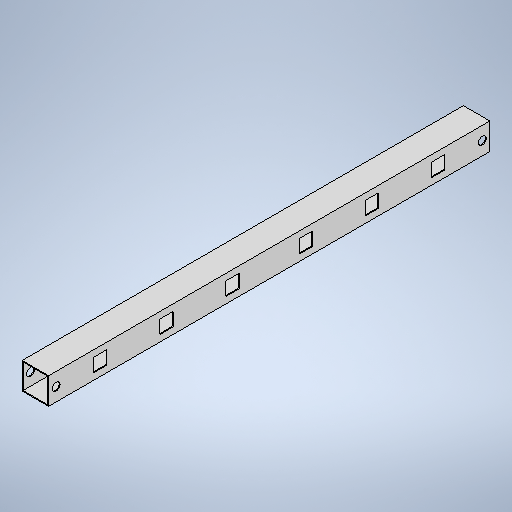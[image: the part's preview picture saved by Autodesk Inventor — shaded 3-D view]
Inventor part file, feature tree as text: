
AUTODESK INVENTOR PART (.ipt)
format: ipt  version: 2025.1 (Build 291241020, 241B)  size: 515,072 bytes
history: native  units: mm
features: sketch x5, extrude x3, projected_geometry x3, fillet x2, mirror x1
ambient origin geometry x8: Origin, YZ Plane, XZ Plane, XY Plane, X Axis, Y Axis, Z Axis, Center Point
bodies: Body1 (feature_tree)
feature tree (14):
  extrude  "Extrusion3"  Depth=60.0mm
  extrude  "Extrusion4"  Depth=2.0mm
  fillet  "Fillet1"  Radius=500.0mm
  mirror  "Mirror1"
  extrude  "Extrusion5"  Depth=30.5mm
  fillet  "Fillet2"  [1 undecoded]
  sketch  "Sketch15"  dims[d181=47.0mm]
  sketch  "Sketch16"  dims[d182=130.0mm d183=280.0mm d184=430.0mm d185=530.0mm d186=18.0mm d187=2.0mm d188=54.0mm d189=500.0mm d190=0.0mm d191=2.0mm]
  sketch  "Sketch9"  dims[d61=500.0mm d172=60.0mm]
  sketch  "Sketch10"  dims[d173=60.0mm d174=2.0mm d175=500.0mm d176=0.0mm]
  projected_geometry  "Projected Loop3"
  sketch  "Sketch14"  dims[d177=30.5mm d178=30.5mm d179=0.0mm d180=0.0mm]
  projected_geometry  "Projected Loop6"
  projected_geometry  "Projected Loop7"
note: 1 required parameter value undecoded (feature->parameter linkage not recoverable at this tier; creation-order binding heuristic only, values carry confidence <= 0.55)
